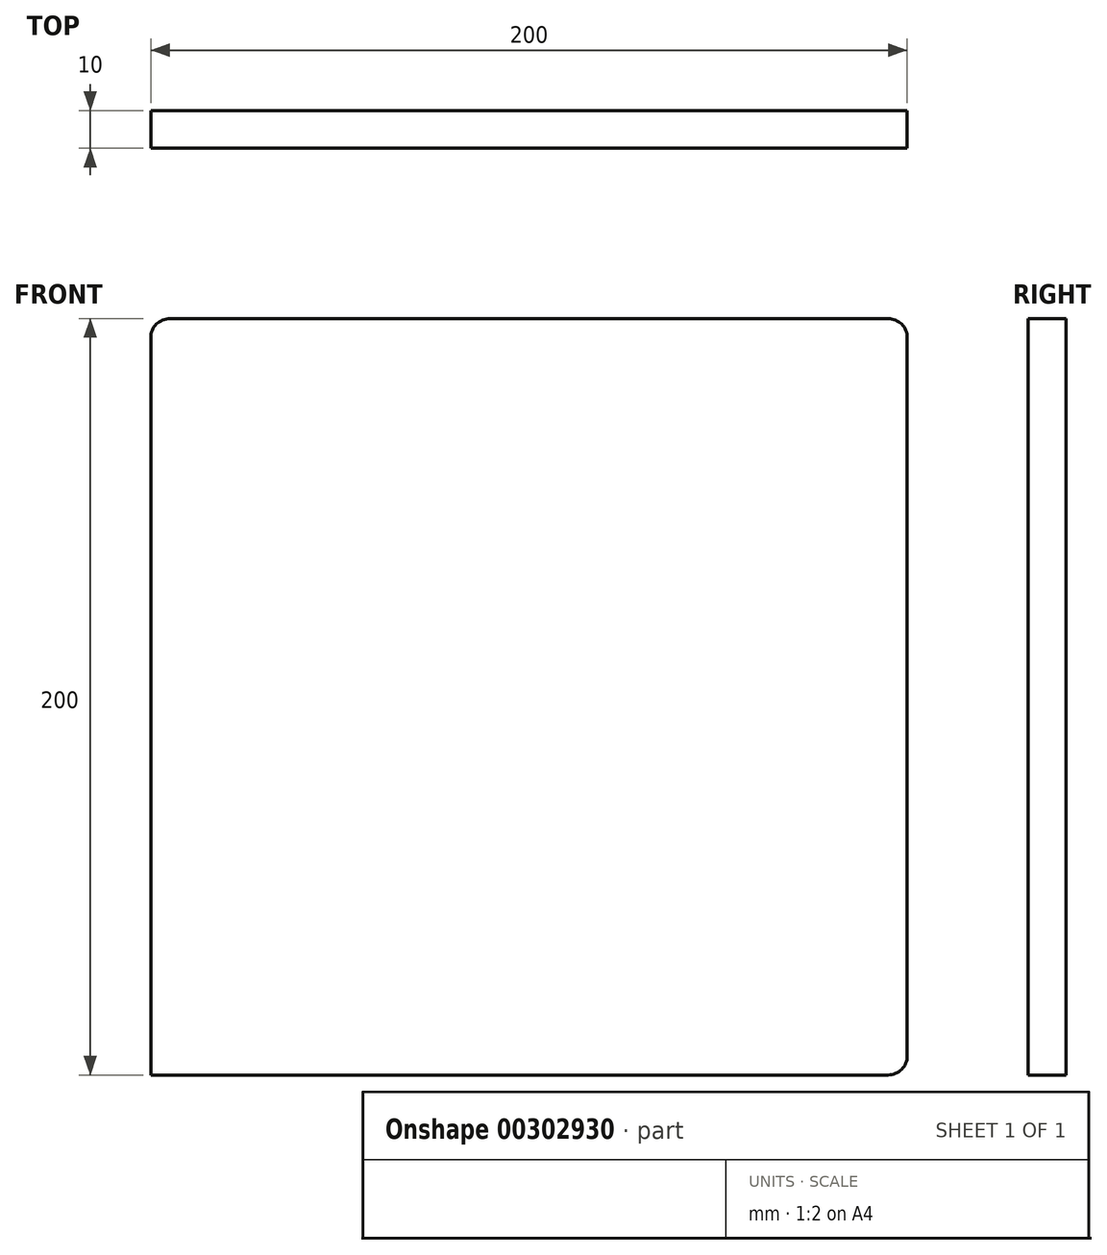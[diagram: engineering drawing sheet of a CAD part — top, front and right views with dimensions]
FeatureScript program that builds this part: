
annotation { "Feature Type Name" : "Feature", "Feature Type Description" : "" }
export const myFeature = defineFeature(function(context is Context, id is Id, definition is map)
    precondition{}
    {
        {
            var Q0;
            Q0=qCreatedBy(makeId("Front.planeOp"),FACE);
            var sketch = newSketch(context, id + "F0", { "sketchPlane" : qUnion([Q0])});
            skLineSegment(sketch, "E0.bottom", {"start": v(100, 100) * mm, "end": v(-100, 100) * mm});
            skLineSegment(sketch, "E0.top", {"start": v(100, -100) * mm, "end": v(-100, -100) * mm});
            skLineSegment(sketch, "E0.left", {"start": v(100, 100) * mm, "end": v(100, -100) * mm});
            skLineSegment(sketch, "E0.right", {"start": v(-100, 100) * mm, "end": v(-100, -100) * mm});
            skPoint(sketch, "E0.middle", {"position": v(0, 0) * mm});
            skSolve(sketch);
        }
        {
            var Q0;
            Q0=makeQuery(id+"F0.imprint","IMPRINT",FACE,{"disambiguationData":[TD([[makeQuery(id+"F0.imprint","IMPRINT",EDGE,{"derivedFrom":sQuery(id+"F0.wireOp",EDGE,"E0.bottom")}),1.0]])]});
            extrude(context, id + "F1", {"entities" : qUnion([Q0]), "depth" : 10 * mm});
        }
        {
            var Q0;
            Q0=makeQuery(id+"F1.opExtrude","CAP_FACE",FACE,{"disambiguationData":[OSD([sQuery(id+"F0.wireOp",EDGE,"E0.bottom"),sQuery(id+"F0.wireOp",EDGE,"E0.top"),sQuery(id+"F0.wireOp",EDGE,"E0.left"),sQuery(id+"F0.wireOp",EDGE,"E0.right")])],"isStart":false});
            var sketch = newSketch(context, id + "F2", { "sketchPlane" : qUnion([Q0])});
            skLineSegment(sketch, "E1.bottom", {"start": v(95, 95) * mm, "end": v(-95, 95) * mm});
            skLineSegment(sketch, "E1.top", {"start": v(95, -95) * mm, "end": v(-95, -95) * mm});
            skLineSegment(sketch, "E1.left", {"start": v(95, 95) * mm, "end": v(95, -95) * mm});
            skLineSegment(sketch, "E1.right", {"start": v(-95, 95) * mm, "end": v(-95, -95) * mm});
            skPoint(sketch, "E1.middle", {"position": v(0, 0) * mm});
            skSolve(sketch);
        }
        {
            var Q0;
            Q0=sQuery(id+"F2.wireOp",EDGE,"E1.bottom");
            var Q1;
            Q1=sQuery(id+"F2.wireOp",EDGE,"E1.left");
            var Q2;
            Q2=sQuery(id+"F2.wireOp",EDGE,"E1.top");
            var Q3;
            Q3=sQuery(id+"F2.wireOp",EDGE,"E1.right");
            extrude(context, id + "F3", {"bodyType" : ToolBodyType.SURFACE, "surfaceEntities" : qUnion([Q0, Q1, Q2, Q3]), "oppositeDirection" : true, "depth" : 200 * mm});
        }
        {
            var Q0;
            Q0=makeQuery(id+"F1.opExtrude","SWEPT_EDGE",EDGE,{"disambiguationData":[OSD([sQuery(id+"F0.wireOp",EDGE,"E0.bottom"),sQuery(id+"F0.wireOp",EDGE,"E0.right")])]});
            var Q1;
            Q1=makeQuery(id+"F1.opExtrude","SWEPT_EDGE",EDGE,{"disambiguationData":[OSD([sQuery(id+"F0.wireOp",EDGE,"E0.top"),sQuery(id+"F0.wireOp",EDGE,"E0.left")])]});
            var Q2;
            Q2=makeQuery(id+"F1.opExtrude","SWEPT_EDGE",EDGE,{"disambiguationData":[OSD([sQuery(id+"F0.wireOp",EDGE,"E0.bottom"),sQuery(id+"F0.wireOp",EDGE,"E0.left")])]});
            fillet(context, id + "F4", {"entities" : qUnion([Q0, Q1, Q2]), "radius" : 5.08 * mm, "tangentPropagation" : true, "allowEdgeOverflow" : false});
        }
        {
            var Q0;
            Q0=makeQuery(id+"F3.opExtrude","SWEPT_FACE",FACE,{"disambiguationData":[OSD([sQuery(id+"F2.wireOp",EDGE,"E1.bottom")])]});
            var sketch = newSketch(context, id + "F5", { "sketchPlane" : qUnion([Q0])});
            skCircle(sketch, "E2", {"center": v(0, -85.84) * mm, "radius": 51.44 * mm});
            skSolve(sketch);
        }
        {
            var Q0;
            Q0=sQuery(id+"F5.wireOp",EDGE,"E2");
            extrude(context, id + "F6", {"bodyType" : ToolBodyType.SURFACE, "surfaceEntities" : qUnion([Q0]), "depth" : 10 * mm});
        }
    });
